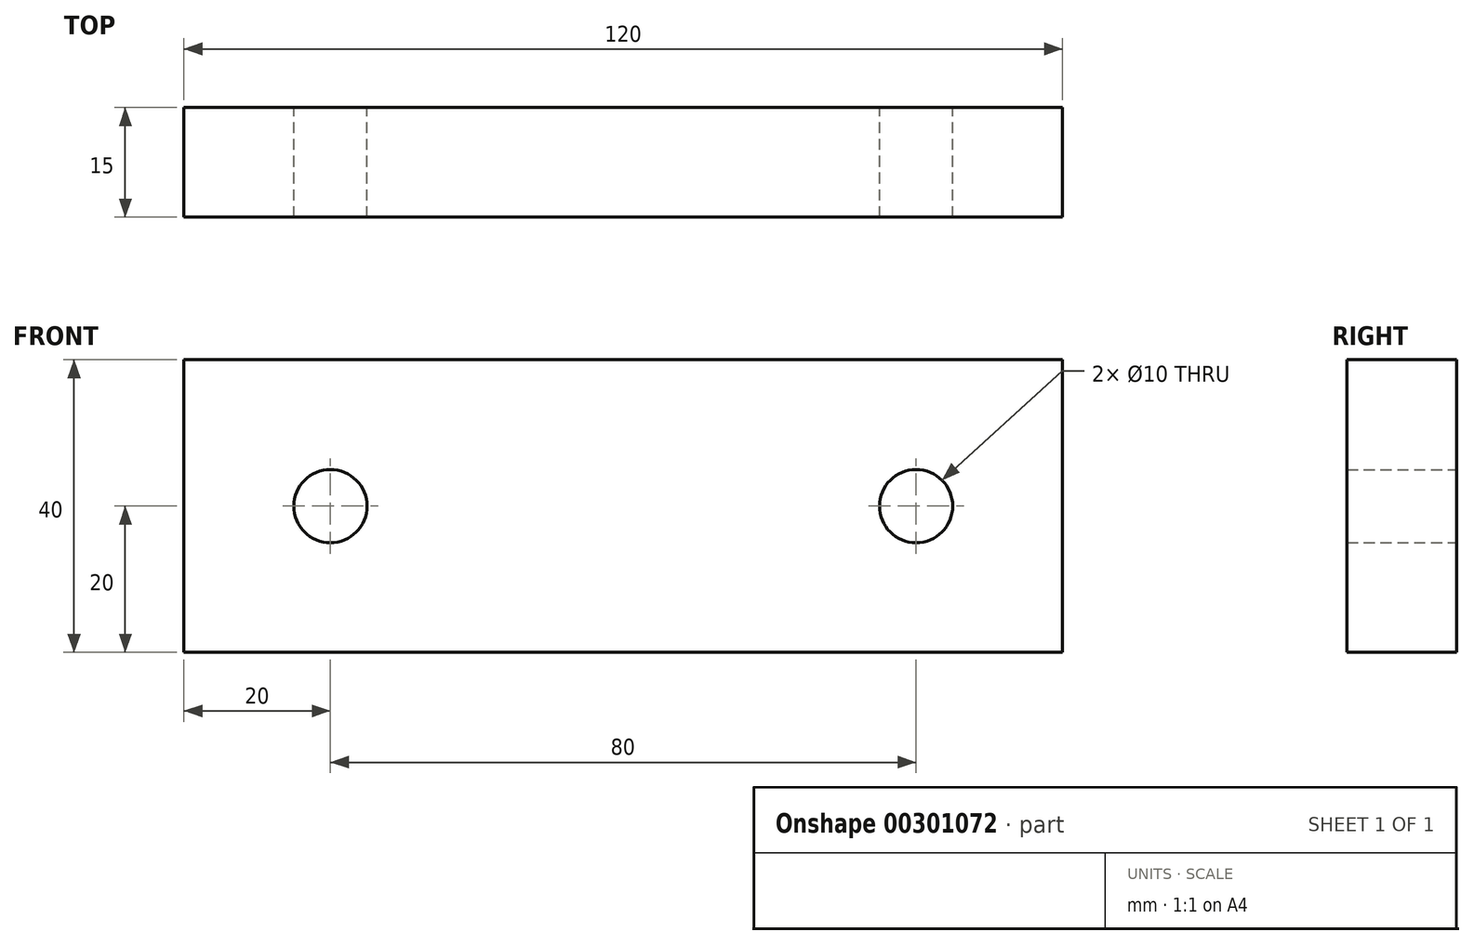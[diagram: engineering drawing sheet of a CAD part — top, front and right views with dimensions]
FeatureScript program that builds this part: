
annotation { "Feature Type Name" : "Feature", "Feature Type Description" : "" }
export const myFeature = defineFeature(function(context is Context, id is Id, definition is map)
    precondition{}
    {
        {
            var Q0;
            Q0=qCreatedBy(makeId("Front.planeOp"),FACE);
            var sketch = newSketch(context, id + "F0", { "sketchPlane" : qUnion([Q0])});
            skLineSegment(sketch, "E0.bottom", {"start": v(0, 0) * mm, "end": v(120, 0) * mm});
            skLineSegment(sketch, "E0.top", {"start": v(0, 40) * mm, "end": v(120, 40) * mm});
            skLineSegment(sketch, "E0.left", {"start": v(0, 0) * mm, "end": v(0, 40) * mm});
            skLineSegment(sketch, "E0.right", {"start": v(120, 0) * mm, "end": v(120, 40) * mm});
            skCircle(sketch, "E1", {"center": v(20, 20) * mm, "radius": 5 * mm});
            skCircle(sketch, "E2", {"center": v(100, 20) * mm, "radius": 5 * mm});
            skSolve(sketch);
        }
        {
            var Q0;
            Q0 = qSketchRegion(id + "F0", true);
            extrude(context, id + "F1", {"entities" : qUnion([Q0]), "depth" : 15 * mm});
        }
    });
